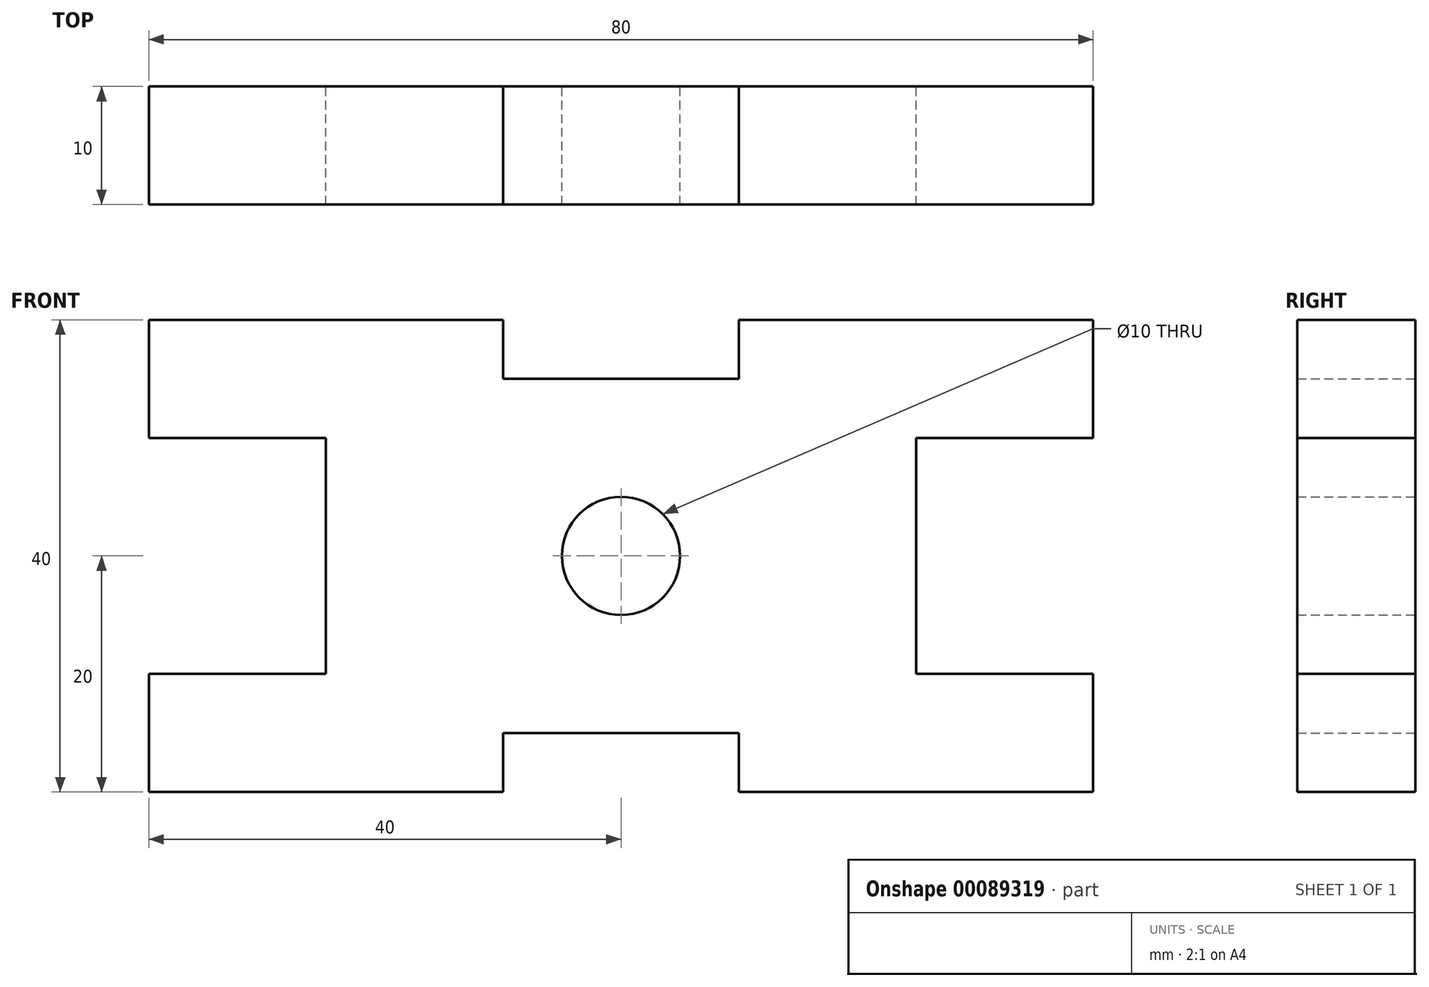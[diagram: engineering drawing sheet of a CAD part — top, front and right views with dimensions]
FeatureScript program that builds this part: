
annotation { "Feature Type Name" : "Feature", "Feature Type Description" : "" }
export const myFeature = defineFeature(function(context is Context, id is Id, definition is map)
    precondition{}
    {
        {
            var Q0;
            Q0=qCreatedBy(makeId("Front.planeOp"),FACE);
            var sketch = newSketch(context, id + "F0", { "sketchPlane" : qUnion([Q0])});
            skArc(sketch, "E0", {"start": v(5, 0) * mm, "mid": v(3.54, 3.54) * mm, "end": v(0, 5) * mm});
            skLineSegment(sketch, "E1", {"start": v(5, 0) * mm, "end": v(25, 0) * mm});
            skLineSegment(sketch, "E2", {"start": v(25, 0) * mm, "end": v(25, 10) * mm});
            skLineSegment(sketch, "E3", {"start": v(25, 10) * mm, "end": v(40, 10) * mm});
            skLineSegment(sketch, "E4", {"start": v(40, 10) * mm, "end": v(40, 20) * mm});
            skLineSegment(sketch, "E5", {"start": v(40, 20) * mm, "end": v(10, 20) * mm});
            skLineSegment(sketch, "E6", {"start": v(10, 20) * mm, "end": v(10, 15) * mm});
            skLineSegment(sketch, "E7", {"start": v(10, 15) * mm, "end": v(0, 15) * mm});
            skLineSegment(sketch, "E8", {"start": v(0, 15) * mm, "end": v(0, 5) * mm});
            skLineSegment(sketch, "E9", {"start": v(0, 52.34) * mm, "end": v(0, -46.17) * mm, "construction": true});
            skPoint(sketch, "E9.startSnap0", {"position": v(0, 10) * mm});
            skLineSegment(sketch, "E10", {"start": v(-54.94, 0) * mm, "end": v(92.92, 0) * mm, "construction": true});
            skLineSegment(sketch, "E11.MirrorCS", {"start": v(40, -20) * mm, "end": v(10, -20) * mm});
            skLineSegment(sketch, "E12.MirrorCS", {"start": v(10, -15) * mm, "end": v(0, -15) * mm});
            skPoint(sketch, "E13.MirrorP", {"position": v(0, -10) * mm});
            skArc(sketch, "E14.MirrorCS", {"start": v(5, 0) * mm, "mid": v(3.54, -3.54) * mm, "end": v(0, -5) * mm});
            skLineSegment(sketch, "E15.MirrorCS", {"start": v(25, 0) * mm, "end": v(25, -10) * mm});
            skLineSegment(sketch, "E16.MirrorCS", {"start": v(25, -10) * mm, "end": v(40, -10) * mm});
            skLineSegment(sketch, "E17.MirrorCS", {"start": v(40, -10) * mm, "end": v(40, -20) * mm});
            skLineSegment(sketch, "E18.MirrorCS", {"start": v(0, -15) * mm, "end": v(0, -5) * mm});
            skLineSegment(sketch, "E19.MirrorCS", {"start": v(0, -15) * mm, "end": v(0, -5) * mm, "construction": true});
            skLineSegment(sketch, "E20.MirrorCS", {"start": v(10, -20) * mm, "end": v(10, -15) * mm});
            skLineSegment(sketch, "E21.MirrorCS", {"start": v(0, 15) * mm, "end": v(0, 5) * mm, "construction": true});
            skLineSegment(sketch, "E22.MirrorCS", {"start": v(-10, 15) * mm, "end": v(0, 15) * mm});
            skArc(sketch, "E23.MirrorCS", {"start": v(-5, 0) * mm, "mid": v(-3.54, -3.54) * mm, "end": v(0, -5) * mm});
            skArc(sketch, "E24.MirrorCS", {"start": v(-5, 0) * mm, "mid": v(-3.54, 3.54) * mm, "end": v(0, 5) * mm});
            skLineSegment(sketch, "E25.MirrorCS", {"start": v(-10, -15) * mm, "end": v(0, -15) * mm});
            skLineSegment(sketch, "E26.MirrorCS", {"start": v(-10, -20) * mm, "end": v(-10, -15) * mm});
            skLineSegment(sketch, "E27.MirrorCS", {"start": v(-40, -20) * mm, "end": v(-10, -20) * mm});
            skLineSegment(sketch, "E28.MirrorCS", {"start": v(-40, -10) * mm, "end": v(-40, -20) * mm});
            skLineSegment(sketch, "E29.MirrorCS", {"start": v(-25, -10) * mm, "end": v(-40, -10) * mm});
            skLineSegment(sketch, "E30.MirrorCS", {"start": v(-25, 0) * mm, "end": v(-25, -10) * mm});
            skLineSegment(sketch, "E31.MirrorCS", {"start": v(54.94, 0) * mm, "end": v(-92.92, 0) * mm, "construction": true});
            skLineSegment(sketch, "E32.MirrorCS", {"start": v(-25, 0) * mm, "end": v(-25, 10) * mm});
            skLineSegment(sketch, "E33.MirrorCS", {"start": v(-25, 10) * mm, "end": v(-40, 10) * mm});
            skLineSegment(sketch, "E34.MirrorCS", {"start": v(-40, 10) * mm, "end": v(-40, 20) * mm});
            skLineSegment(sketch, "E35.MirrorCS", {"start": v(-40, 20) * mm, "end": v(-10, 20) * mm});
            skLineSegment(sketch, "E36.MirrorCS", {"start": v(-10, 20) * mm, "end": v(-10, 15) * mm});
            skSolve(sketch);
        }
        {
            var Q0;
            Q0 = qSketchRegion(id + "F0", true);
            extrude(context, id + "F1", {"entities" : qUnion([Q0]), "depth" : 10 * mm});
        }
    });
